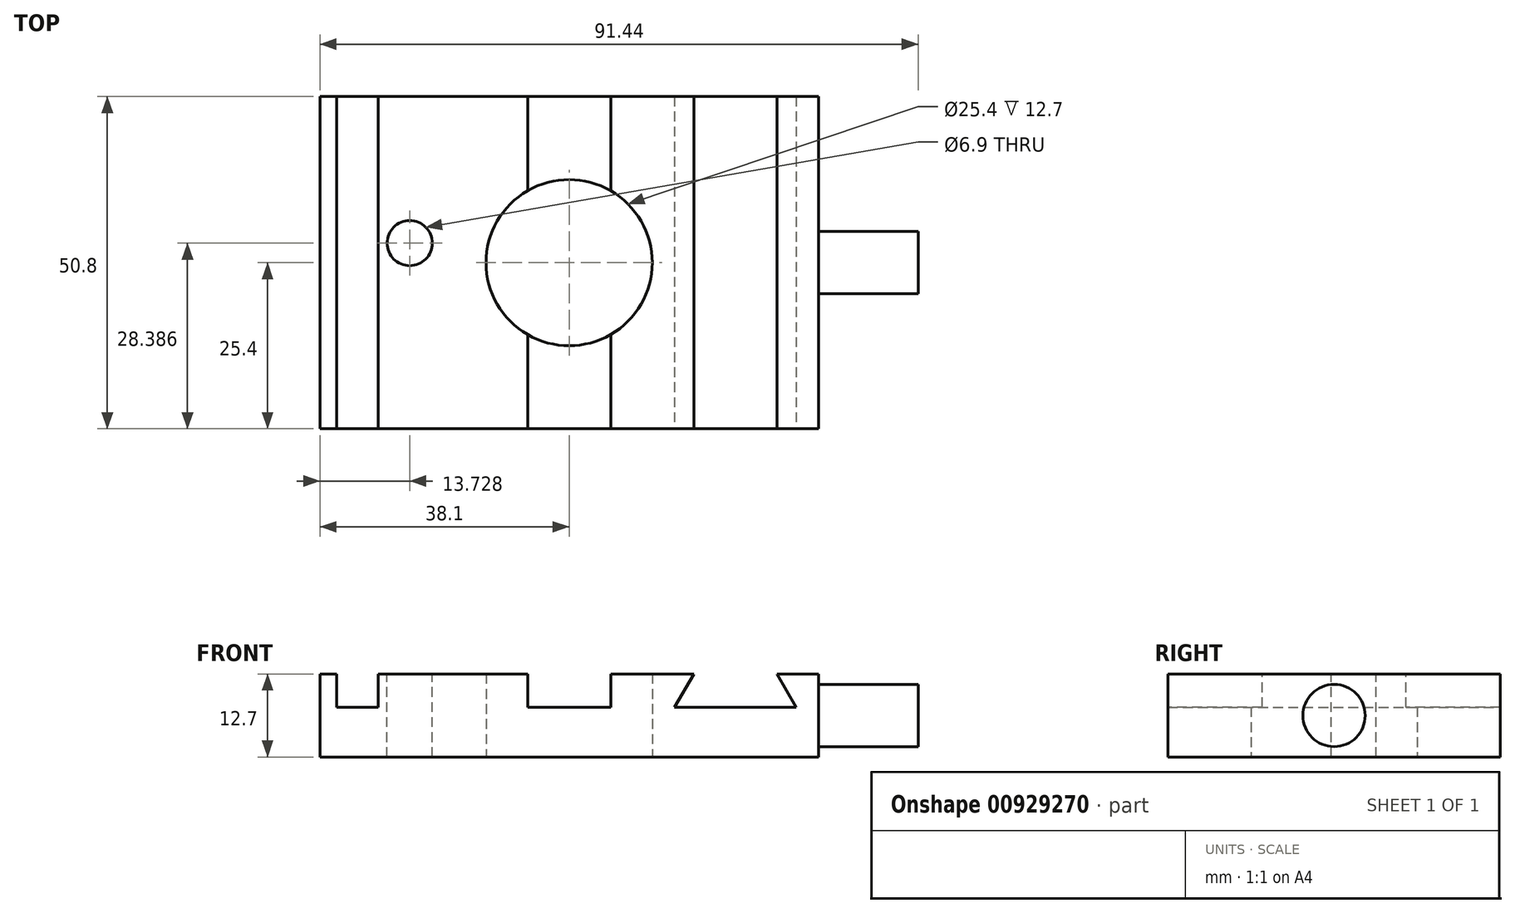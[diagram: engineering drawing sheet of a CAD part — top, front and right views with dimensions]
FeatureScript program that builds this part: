
annotation { "Feature Type Name" : "Feature", "Feature Type Description" : "" }
export const myFeature = defineFeature(function(context is Context, id is Id, definition is map)
    precondition{}
    {
        {
            var Q0;
            Q0=qCreatedBy(makeId("Top.planeOp"),FACE);
            var sketch = newSketch(context, id + "F0", { "sketchPlane" : qUnion([Q0])});
            skLineSegment(sketch, "E0.bottom", {"start": v(-38.1, 25.4) * mm, "end": v(38.1, 25.4) * mm});
            skLineSegment(sketch, "E0.top", {"start": v(-38.1, -25.4) * mm, "end": v(38.1, -25.4) * mm});
            skLineSegment(sketch, "E0.left", {"start": v(-38.1, 25.4) * mm, "end": v(-38.1, -25.4) * mm});
            skLineSegment(sketch, "E0.right", {"start": v(38.1, 25.4) * mm, "end": v(38.1, -25.4) * mm});
            skPoint(sketch, "E0.middle", {"position": v(0, 0) * mm});
            skCircle(sketch, "E1", {"center": v(0, 0) * mm, "radius": 12.7 * mm});
            skSolve(sketch);
        }
        {
            var Q0;
            Q0=makeQuery(id+"F0.imprint","IMPRINT",FACE,{"disambiguationData":[TD([[makeQuery(id+"F0.imprint","IMPRINT",EDGE,{"derivedFrom":sQuery(id+"F0.wireOp",EDGE,"E0.bottom")}),-1.0]])]});
            extrude(context, id + "F1", {"entities" : qUnion([Q0]), "depth" : 12.7 * mm, "offsetDistance" : 25.4 * mm});
        }
        {
            var Q0;
            Q0=makeQuery(id+"F1.opExtrude","CAP_FACE",FACE,{"disambiguationData":[OSD([sQuery(id+"F0.wireOp",EDGE,"E0.bottom"),sQuery(id+"F0.wireOp",EDGE,"E0.top"),sQuery(id+"F0.wireOp",EDGE,"E0.left"),sQuery(id+"F0.wireOp",EDGE,"E0.right"),sQuery(id+"F0.wireOp",EDGE,"E1")])],"isStart":false});
            var sketch = newSketch(context, id + "F2", { "sketchPlane" : qUnion([Q0])});
            skLineSegment(sketch, "E2.bottom", {"start": v(-35.56, -25.4) * mm, "end": v(-29.21, -25.4) * mm});
            skLineSegment(sketch, "E2.top", {"start": v(-35.56, 25.4) * mm, "end": v(-29.21, 25.4) * mm});
            skLineSegment(sketch, "E2.left", {"start": v(-35.56, -25.4) * mm, "end": v(-35.56, 25.4) * mm});
            skLineSegment(sketch, "E2.right", {"start": v(-29.21, -25.4) * mm, "end": v(-29.21, 25.4) * mm});
            skLineSegment(sketch, "E3", {"start": v(-6.35, 25.4) * mm, "end": v(-6.35, -25.4) * mm});
            skLineSegment(sketch, "E4", {"start": v(-6.35, -25.4) * mm, "end": v(6.35, -25.4) * mm});
            skLineSegment(sketch, "E5", {"start": v(6.35, -25.4) * mm, "end": v(6.35, 25.4) * mm});
            skLineSegment(sketch, "E6", {"start": v(6.35, 25.4) * mm, "end": v(-6.35, 25.4) * mm});
            skPoint(sketch, "E7", {"position": v(0, 0) * mm});
            skLineSegment(sketch, "E8", {"start": v(0, 25.4) * mm, "end": v(0, -25.4) * mm, "construction": true});
            skSolve(sketch);
        }
        {
            var Q0;
            Q0=makeQuery(id+"F2.imprint","IMPRINT",FACE,{"disambiguationData":[TD([[makeQuery(id+"F2.imprint","IMPRINT",EDGE,{"derivedFrom":sQuery(id+"F2.wireOp",EDGE,"E2.bottom")}),1.0]])]});
            var Q1;
            {var subQ0=sQuery(id+"F2.wireOp",EDGE,"E6");Q1=makeQuery(id+"F2.imprint","IMPRINT",FACE,{"disambiguationData":[TD([[makeQuery(id+"F2.imprint","IMPRINT",EDGE,{"derivedFrom":subQ0}),-1.0]])]});}
            var Q2;
            {var subQ0=sQuery(id+"F2.wireOp",EDGE,"E4");Q2=makeQuery(id+"F2.imprint","IMPRINT",FACE,{"disambiguationData":[TD([[makeQuery(id+"F2.imprint","IMPRINT",EDGE,{"derivedFrom":subQ0}),1.0]])]});}
            extrude(context, id + "F3", {"entities" : qUnion([Q0, Q1, Q2]), "operationType" : NewBodyOperationType.REMOVE, "oppositeDirection" : true, "depth" : 5.08 * mm, "offsetDistance" : 25.4 * mm});
        }
        {
            var Q0;
            Q0=makeQuery(id+"F1.opExtrude","SWEPT_FACE",FACE,{"disambiguationData":[OSD([sQuery(id+"F0.wireOp",EDGE,"E0.top")])]});
            var sketch = newSketch(context, id + "F4", { "sketchPlane" : qUnion([Q0])});
            skLineSegment(sketch, "E9", {"start": v(6.6, 7.62) * mm, "end": v(6.6, 7.62) * mm});
            skLineSegment(sketch, "E10", {"start": v(19.05, 12.7) * mm, "end": v(16.12, 7.62) * mm});
            skLineSegment(sketch, "E11", {"start": v(16.12, 7.62) * mm, "end": v(34.68, 7.62) * mm});
            skLineSegment(sketch, "E12", {"start": v(34.68, 7.62) * mm, "end": v(31.75, 12.7) * mm});
            skLineSegment(sketch, "E13", {"start": v(31.75, 12.7) * mm, "end": v(19.05, 12.7) * mm});
            skLineSegment(sketch, "E14", {"start": v(25.4, 7.62) * mm, "end": v(25.4, 12.7) * mm, "construction": true});
            skSolve(sketch);
        }
        {
            var Q0;
            Q0=makeQuery(id+"F4.imprint","IMPRINT",FACE,{"disambiguationData":[TD([[makeQuery(id+"F4.imprint","IMPRINT",EDGE,{"derivedFrom":sQuery(id+"F4.wireOp",EDGE,"E10")}),1.0]])]});
            extrude(context, id + "F5", {"entities" : qUnion([Q0]), "operationType" : NewBodyOperationType.REMOVE, "endBound" : BoundingType.THROUGH_ALL, "oppositeDirection" : true, "depth" : 25.4 * mm, "offsetDistance" : 25.4 * mm});
        }
        {
            var Q0;
            Q0=makeQuery(id+"F1.opExtrude","SWEPT_FACE",FACE,{"disambiguationData":[OSD([sQuery(id+"F0.wireOp",EDGE,"E0.right")])]});
            var sketch = newSketch(context, id + "F6", { "sketchPlane" : qUnion([Q0])});
            skCircle(sketch, "E15", {"center": v(0, 6.35) * mm, "radius": 4.76 * mm});
            skPoint(sketch, "E15.centerSnap0", {"position": v(-25.4, 6.35) * mm});
            skPoint(sketch, "E15.centerSnap1", {"position": v(0, 12.7) * mm});
            skSolve(sketch);
        }
        {
            var Q0;
            Q0=makeQuery(id+"F6.imprint","IMPRINT",FACE,{"disambiguationData":[TD([[makeQuery(id+"F6.imprint","IMPRINT",EDGE,{"derivedFrom":sQuery(id+"F6.wireOp",EDGE,"E15")}),1.0]])]});
            extrude(context, id + "F7", {"entities" : qUnion([Q0]), "operationType" : NewBodyOperationType.ADD, "depth" : 15.24 * mm, "offsetDistance" : 25.4 * mm});
        }
        {
            var Q0;
            {var subQ0=sQuery(id+"F0.wireOp",EDGE,"E1");var subQ1=sQuery(id+"F0.wireOp",EDGE,"E0.top");var subQ2=sQuery(id+"F0.wireOp",EDGE,"E0.bottom");Q0=makeQuery(id+"F3.boolean.opBoolean","SPLIT",FACE,{"disambiguationData":[TD([makeQuery(id+"F3.opExtrude","SWEPT_FACE",FACE,{"disambiguationData":[OSD([sQuery(id+"F2.wireOp",EDGE,"E2.right")])]})])],"derivedFrom":makeQuery(id+"F1.opExtrude","CAP_FACE",FACE,{"disambiguationData":[OSD([subQ2,subQ1,sQuery(id+"F0.wireOp",EDGE,"E0.left"),sQuery(id+"F0.wireOp",EDGE,"E0.right"),subQ0])],"isStart":false})});}
            var sketch = newSketch(context, id + "F8", { "sketchPlane" : qUnion([Q0])});
            skCircle(sketch, "E16", {"center": v(-24.37, 2.99) * mm, "radius": 3.45 * mm});
            skSolve(sketch);
        }
        {
            var Q0;
            Q0 = qSketchRegion(id + "F8", true);
            extrude(context, id + "F9", {"entities" : qUnion([Q0]), "operationType" : NewBodyOperationType.REMOVE, "endBound" : BoundingType.THROUGH_ALL, "oppositeDirection" : true, "depth" : 25.4 * mm, "offsetDistance" : 25.4 * mm});
        }
        {
            var Q0;
            {var subQ0=sQuery(id+"F0.wireOp",EDGE,"E1");var subQ1=sQuery(id+"F0.wireOp",EDGE,"E0.top");var subQ2=sQuery(id+"F0.wireOp",EDGE,"E0.bottom");Q0=makeQuery(id+"F3.boolean.opBoolean","SPLIT",FACE,{"disambiguationData":[TD([makeQuery(id+"F3.opExtrude","SWEPT_FACE",FACE,{"disambiguationData":[OSD([sQuery(id+"F2.wireOp",EDGE,"E2.right")])]})])],"derivedFrom":makeQuery(id+"F1.opExtrude","CAP_FACE",FACE,{"disambiguationData":[OSD([subQ2,subQ1,sQuery(id+"F0.wireOp",EDGE,"E0.left"),sQuery(id+"F0.wireOp",EDGE,"E0.right"),subQ0])],"isStart":false})});}
            var sketch = newSketch(context, id + "F10", { "sketchPlane" : qUnion([Q0])});
            skCircle(sketch, "E17", {"center": v(-21, -11.73) * mm, "radius": 4.21 * mm});
            skSolve(sketch);
        }
        {
            var Q0;
            Q0 = qSketchRegion(id + "F10", true);
            extrude(context, id + "F11", {"entities" : qUnion([Q0]), "operationType" : NewBodyOperationType.REMOVE, "endBound" : BoundingType.THROUGH_ALL, "depth" : 25.4 * mm, "offsetDistance" : 25.4 * mm});
        }
    });
